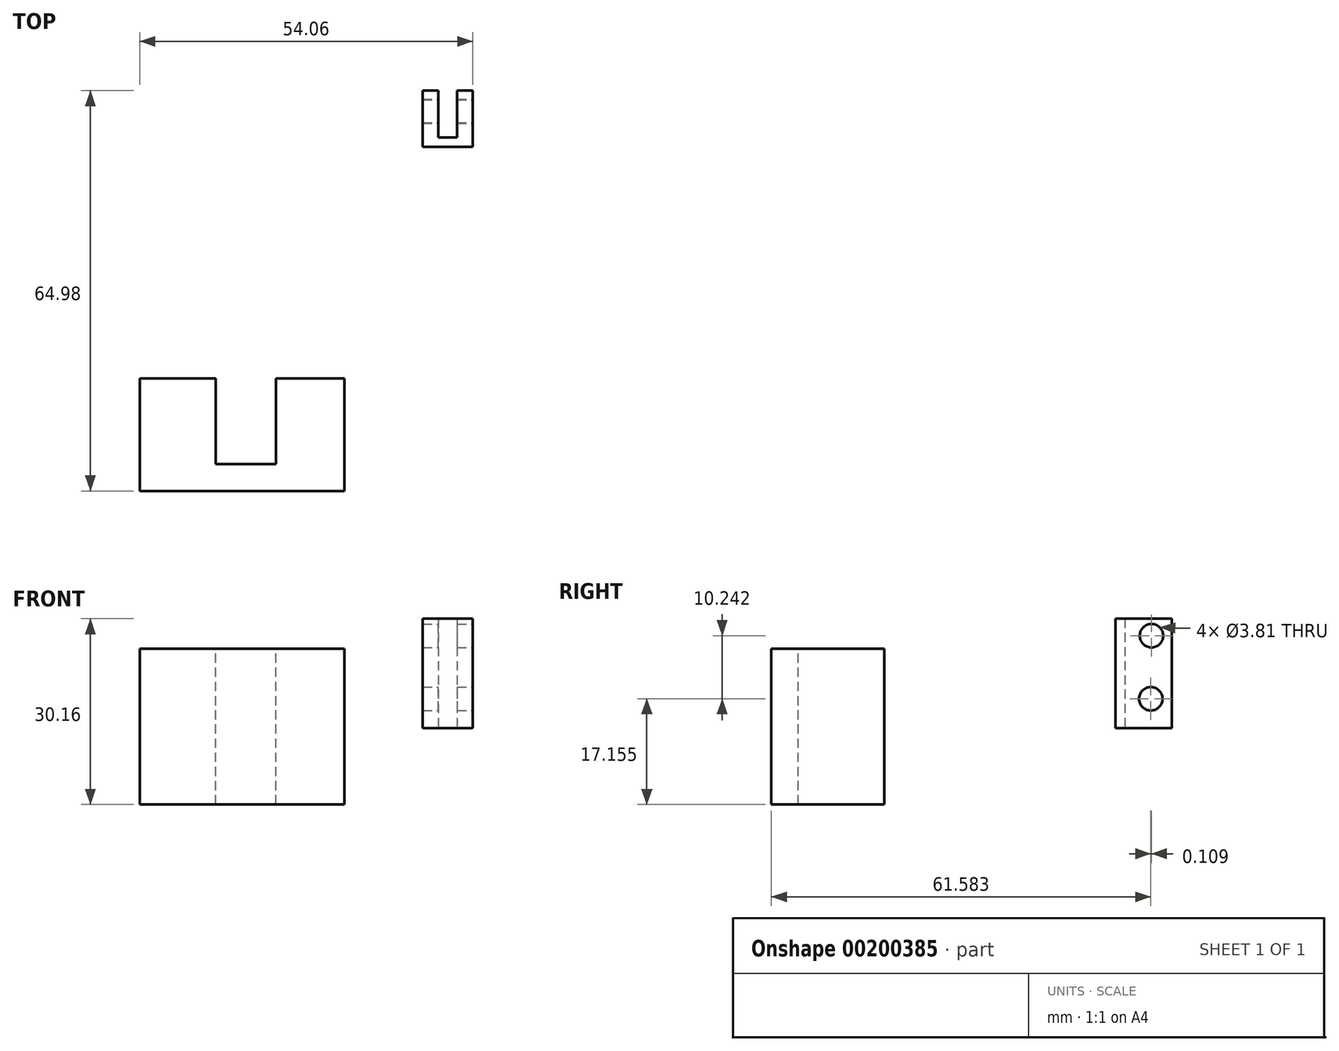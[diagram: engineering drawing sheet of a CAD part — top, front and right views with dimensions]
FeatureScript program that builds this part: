
annotation { "Feature Type Name" : "Feature", "Feature Type Description" : "" }
export const myFeature = defineFeature(function(context is Context, id is Id, definition is map)
    precondition{}
    {
        {
            var Q0;
            Q0=qCreatedBy(makeId("Front.planeOp"),FACE);
            var sketch = newSketch(context, id + "F0", { "sketchPlane" : qUnion([Q0])});
            skLineSegment(sketch, "E0.bottom", {"start": v(-12.3, 12.9) * mm, "end": v(20.91, 12.9) * mm});
            skLineSegment(sketch, "E0.top", {"start": v(-12.3, -12.38) * mm, "end": v(20.91, -12.38) * mm});
            skLineSegment(sketch, "E0.left", {"start": v(-12.3, 12.9) * mm, "end": v(-12.3, -12.38) * mm});
            skLineSegment(sketch, "E0.right", {"start": v(20.91, 12.9) * mm, "end": v(20.91, -12.38) * mm});
            skSolve(sketch);
        }
        {
            var Q0;
            Q0 = qSketchRegion(id + "F0", true);
            extrude(context, id + "F1", {"entities" : qUnion([Q0]), "depth" : 18.29 * mm});
        }
        {
            var Q0;
            Q0=makeQuery(id+"F1.opExtrude","SWEPT_FACE",FACE,{"disambiguationData":[OSD([sQuery(id+"F0.wireOp",EDGE,"E0.bottom")])]});
            var sketch = newSketch(context, id + "F2", { "sketchPlane" : qUnion([Q0])});
            skLineSegment(sketch, "E1.bottom", {"start": v(0, 0) * mm, "end": v(0, 0) * mm});
            skLineSegment(sketch, "E1.top", {"start": v(0, -13.96) * mm, "end": v(0, -13.96) * mm});
            skLineSegment(sketch, "E1.left", {"start": v(0, 0) * mm, "end": v(0, -13.96) * mm});
            skLineSegment(sketch, "E1.right", {"start": v(0, 0) * mm, "end": v(0, -13.96) * mm});
            skLineSegment(sketch, "E2.top", {"start": v(0, -2.58) * mm, "end": v(0, -2.58) * mm});
            skLineSegment(sketch, "E2.left", {"start": v(0, -13.96) * mm, "end": v(0, -2.58) * mm});
            skLineSegment(sketch, "E2.right", {"start": v(0, -13.96) * mm, "end": v(0, -2.58) * mm});
            skLineSegment(sketch, "E3.bottom", {"start": v(0, 0) * mm, "end": v(9.8, 0) * mm});
            skLineSegment(sketch, "E3.top", {"start": v(0, -13.96) * mm, "end": v(9.8, -13.96) * mm});
            skLineSegment(sketch, "E3.right", {"start": v(9.8, 0) * mm, "end": v(9.8, -13.96) * mm});
            skSolve(sketch);
        }
        {
            var Q0;
            {var subQ3=sQuery(id+"F2.wireOp",EDGE,"E3.bottom");Q0=makeQuery(id+"F2.imprint","IMPRINT",FACE,{"disambiguationData":[TD([[makeQuery(id+"F2.imprint","IMPRINT",EDGE,{"derivedFrom":subQ3}),-1.0]])]});}
            extrude(context, id + "F3", {"entities" : qUnion([Q0]), "operationType" : NewBodyOperationType.REMOVE, "oppositeDirection" : true, "depth" : 25.4 * mm});
        }
        {
            var Q0;
            Q0=qCreatedBy(makeId("Top.planeOp"),FACE);
            var sketch = newSketch(context, id + "F4", { "sketchPlane" : qUnion([Q0])});
            skLineSegment(sketch, "E4.bottom", {"start": v(33.63, 46.7) * mm, "end": v(36.17, 46.7) * mm});
            skLineSegment(sketch, "E4.top", {"start": v(33.63, 37.55) * mm, "end": v(36.17, 37.55) * mm});
            skLineSegment(sketch, "E4.left", {"start": v(33.63, 46.7) * mm, "end": v(33.63, 37.55) * mm});
            skLineSegment(sketch, "E4.right", {"start": v(36.17, 46.7) * mm, "end": v(36.17, 37.55) * mm});
            skLineSegment(sketch, "E5.bottom", {"start": v(36.17, 39.07) * mm, "end": v(39.21, 39.07) * mm});
            skLineSegment(sketch, "E5.top", {"start": v(36.17, 37.55) * mm, "end": v(39.21, 37.55) * mm});
            skLineSegment(sketch, "E5.left", {"start": v(36.17, 39.07) * mm, "end": v(36.17, 37.55) * mm});
            skLineSegment(sketch, "E5.right", {"start": v(39.21, 39.07) * mm, "end": v(39.21, 37.55) * mm});
            skLineSegment(sketch, "E6.bottom", {"start": v(39.21, 37.55) * mm, "end": v(41.75, 37.55) * mm});
            skLineSegment(sketch, "E6.top", {"start": v(39.21, 46.7) * mm, "end": v(41.75, 46.7) * mm});
            skLineSegment(sketch, "E6.left", {"start": v(39.21, 37.55) * mm, "end": v(39.21, 46.7) * mm});
            skLineSegment(sketch, "E6.right", {"start": v(41.75, 37.55) * mm, "end": v(41.75, 46.7) * mm});
            skSolve(sketch);
        }
        {
            var Q0;
            Q0=makeQuery(id+"F4.imprint","IMPRINT",FACE,{"disambiguationData":[TD([[makeQuery(id+"F4.imprint","IMPRINT",EDGE,{"derivedFrom":sQuery(id+"F4.wireOp",EDGE,"E4.bottom")}),-1.0]])]});
            var Q1;
            {var subQ0=sQuery(id+"F4.wireOp",EDGE,"E5.bottom");Q1=makeQuery(id+"F4.imprint","IMPRINT",FACE,{"disambiguationData":[TD([[makeQuery(id+"F4.imprint","IMPRINT",EDGE,{"derivedFrom":subQ0}),-1.0]])]});}
            var Q2;
            {var subQ2=sQuery(id+"F4.wireOp",EDGE,"E6.bottom");Q2=makeQuery(id+"F4.imprint","IMPRINT",FACE,{"disambiguationData":[TD([[makeQuery(id+"F4.imprint","IMPRINT",EDGE,{"derivedFrom":subQ2}),1.0]])]});}
            extrude(context, id + "F5", {"entities" : qUnion([Q0, Q1, Q2]), "depth" : 17.78 * mm});
        }
        {
            var Q0;
            Q0=makeQuery(id+"F5.opExtrude","SWEPT_FACE",FACE,{"disambiguationData":[OSD([sQuery(id+"F4.wireOp",EDGE,"E6.right")])]});
            var sketch = newSketch(context, id + "F6", { "sketchPlane" : qUnion([Q0])});
            skCircle(sketch, "E7", {"center": v(43.4, 15.02) * mm, "radius": 1.9 * mm});
            skCircle(sketch, "E8", {"center": v(43.3, 4.77) * mm, "radius": 1.9 * mm});
            skSolve(sketch);
        }
        {
            var Q0;
            Q0 = qSketchRegion(id + "F6", true);
            extrude(context, id + "F7", {"entities" : qUnion([Q0]), "operationType" : NewBodyOperationType.REMOVE, "oppositeDirection" : true, "depth" : 25.4 * mm});
        }
    });
